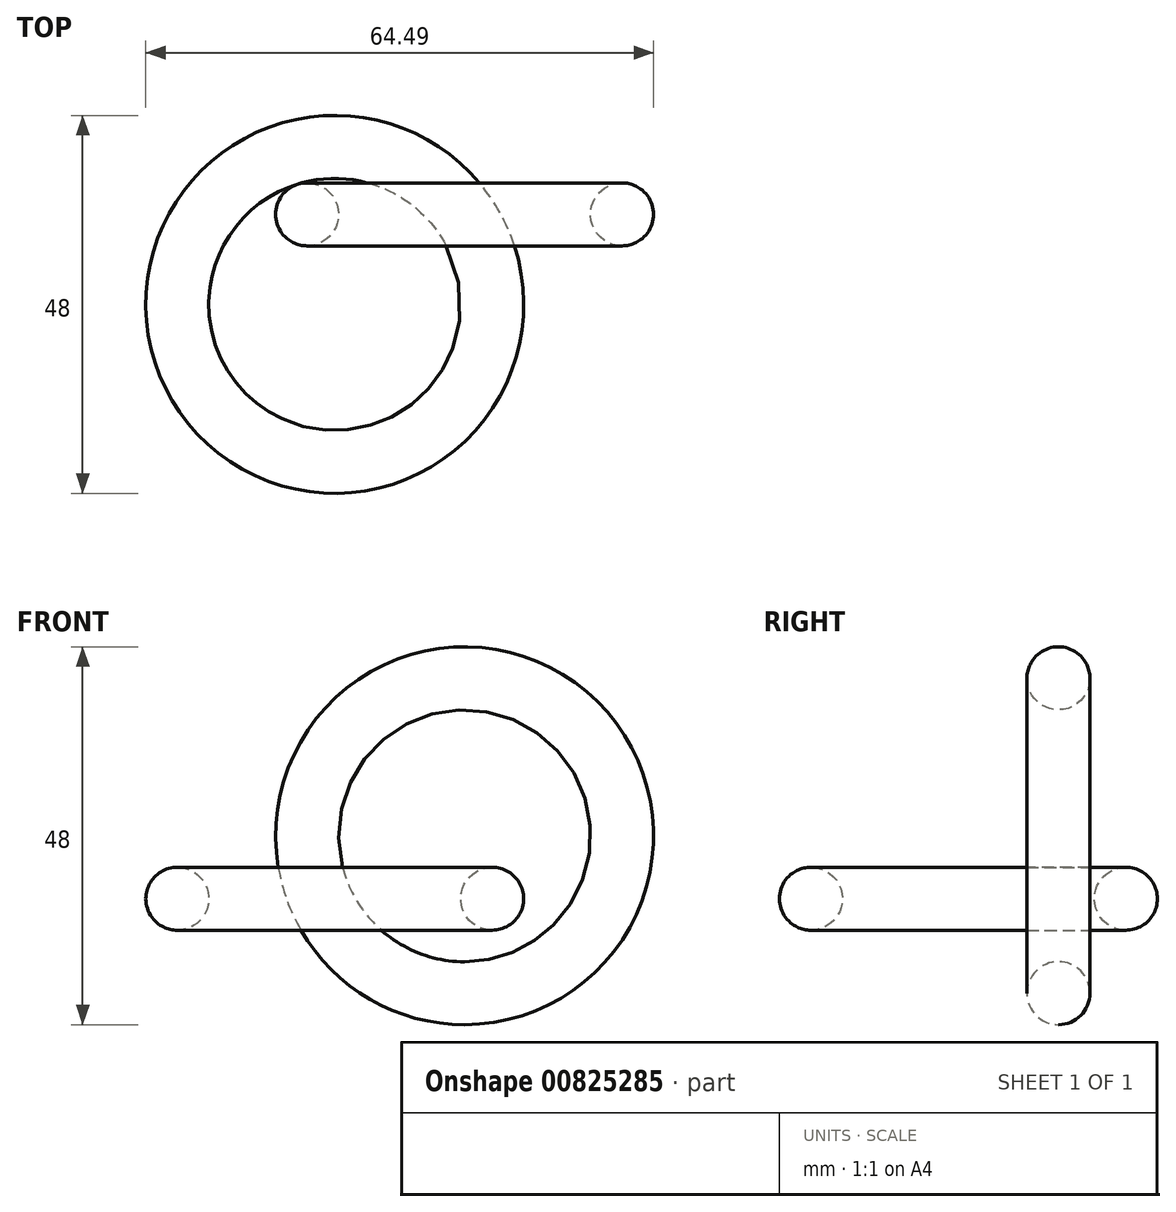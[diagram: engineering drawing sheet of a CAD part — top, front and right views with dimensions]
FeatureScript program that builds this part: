
annotation { "Feature Type Name" : "Feature", "Feature Type Description" : "" }
export const myFeature = defineFeature(function(context is Context, id is Id, definition is map)
    precondition{}
    {
        {
            var Q0;
            Q0=qCreatedBy(makeId("Top.planeOp"),FACE);
            var sketch = newSketch(context, id + "F0", { "sketchPlane" : qUnion([Q0])});
            skLineSegment(sketch, "E0", {"start": v(0, 0) * mm, "end": v(20, 0) * mm, "construction": true});
            skCircle(sketch, "E1", {"center": v(20, 0) * mm, "radius": 4 * mm});
            skSolve(sketch);
        }
        {
            var Q0;
            Q0=qCreatedBy(makeId("Front.planeOp"),FACE);
            var sketch = newSketch(context, id + "F1", { "sketchPlane" : qUnion([Q0])});
            skCircle(sketch, "E2", {"center": v(0, 0) * mm, "radius": 17.63 * mm});
            skSolve(sketch);
        }
        {
            var Q0;
            Q0=makeQuery(id+"F0.imprint","IMPRINT",FACE,{"disambiguationData":[TD([[makeQuery(id+"F0.imprint","IMPRINT",EDGE,{"derivedFrom":sQuery(id+"F0.wireOp",EDGE,"E1")}),1.0]])]});
            var Q1;
            Q1=sQuery(id+"F1.wireOp",EDGE,"E2");
            sweep(context, id + "F2", {"profiles" : qUnion([Q0]), "path" : qUnion([Q1])});
        }
        {
            var Q0;
            Q0=qCreatedBy(makeId("Front.planeOp"),FACE);
            var sketch = newSketch(context, id + "F3", { "sketchPlane" : qUnion([Q0])});
            skLineSegment(sketch, "E3", {"start": v(0, 0) * mm, "end": v(0, -1) * mm, "construction": true});
            skLineSegment(sketch, "E4.bottom", {"start": v(0, -1) * mm, "end": v(4, -1) * mm});
            skLineSegment(sketch, "E4.right", {"start": v(4, -1) * mm, "end": v(4, -21) * mm});
            skLineSegment(sketch, "E5.bottom", {"start": v(0, -1) * mm, "end": v(-4, -1) * mm});
            skLineSegment(sketch, "E5.top", {"start": v(0, -21) * mm, "end": v(-4, -21) * mm});
            skLineSegment(sketch, "E5.right", {"start": v(-4, -1) * mm, "end": v(-4, -21) * mm});
            skLineSegment(sketch, "E6", {"start": v(4, -21) * mm, "end": v(-4, -21) * mm});
            skSolve(sketch);
        }
        {
            var Q0;
            Q0=makeQuery(id+"F3.imprint","IMPRINT",FACE,{"disambiguationData":[TD([[makeQuery(id+"F3.imprint","IMPRINT",EDGE,{"derivedFrom":sQuery(id+"F3.wireOp",EDGE,"E4.bottom")}),-1.0]])]});
            extrude(context, id + "F4", {"entities" : qUnion([Q0]), "endBound" : BoundingType.SYMMETRIC, "oppositeDirection" : true, "depth" : 8 * mm, "offsetDistance" : 25 * mm});
        }
        {
            var Q0;
            Q0=makeQuery(id+"F4.opExtrude","CAP_EDGE",EDGE,{"disambiguationData":[OSD([sQuery(id+"F3.wireOp",EDGE,"E5.right")])],"isStart":false});
            chamfer(context, id + "F5", {"entities" : qUnion([Q0]), "width" : 8 * mm, "tangentPropagation" : true});
        }
        {
            var Q0;
            Q0=makeQuery(id+"F5.opChamfer","BLEND_FACE",FACE,{"disambiguationData":[OSD([sQuery(id+"F3.wireOp",EDGE,"E5.right")])]});
            var sketch = newSketch(context, id + "F6", { "sketchPlane" : qUnion([Q0])});
            skLineSegment(sketch, "E7", {"start": v(0, 0) * mm, "end": v(0, -8) * mm, "construction": true});
            skCircle(sketch, "E8", {"center": v(0, -8) * mm, "radius": 4 * mm});
            skSolve(sketch);
        }
        {
            var Q0;
            Q0=makeQuery(id+"F4.opExtrude","SWEPT_FACE",FACE,{"disambiguationData":[OSD([sQuery(id+"F3.wireOp",EDGE,"E6")])]});
            var sketch = newSketch(context, id + "F7", { "sketchPlane" : qUnion([Q0])});
            skLineSegment(sketch, "E9", {"start": v(0, 0) * mm, "end": v(-14.14, 14.14) * mm, "construction": true});
            skCircle(sketch, "E10", {"center": v(-14.14, 14.14) * mm, "radius": 20 * mm});
            skSolve(sketch);
        }
        {
            var Q0;
            {var subQ0=sQuery(id+"F6.wireOp",EDGE,"E8");var subQ1=makeQuery(id+"F5.opChamfer","BLEND_EDGE",EDGE,{"blendedFrom":[makeQuery(id+"F4.opExtrude","CAP_EDGE",EDGE,{"disambiguationData":[OSD([sQuery(id+"F3.wireOp",EDGE,"E5.right")])],"isStart":false}),makeQuery(id+"F4.opExtrude","SWEPT_FACE",FACE,{"disambiguationData":[OSD([sQuery(id+"F3.wireOp",EDGE,"E4.bottom"),sQuery(id+"F3.wireOp",EDGE,"E5.bottom")])]})],"blendedInto":[makeQuery(id+"F4.opExtrude","SWEPT_FACE",FACE,{"disambiguationData":[OSD([sQuery(id+"F3.wireOp",EDGE,"E4.bottom"),sQuery(id+"F3.wireOp",EDGE,"E5.bottom")])]})]});var subQ2=makeQuery(id+"F6.imprint","INTERSECT",VERTEX,{"disambiguationData":[OD(0.0)],"derivedFrom":[subQ1,subQ0]});Q0=makeQuery(id+"F6.imprint","IMPRINT",FACE,{"disambiguationData":[TD([[makeQuery(id+"F6.imprint","IMPRINT",EDGE,{"disambiguationData":[TD([[subQ2,1.0]])],"derivedFrom":subQ0}),1.0]])]});}
            var Q1;
            Q1=sQuery(id+"F7.wireOp",EDGE,"E10");
            sweep(context, id + "F8", {"profiles" : qUnion([Q0]), "path" : qUnion([Q1])});
        }
        {
            var Q0;
            Q0=makeQuery(id+"F8.opSweep","SWEPT_BODY",BODY,{"disambiguationData":[OSD([sQuery(id+"F6.wireOp",EDGE,"E8"),sQuery(id+"F7.wireOp",EDGE,"E10")])]});
            var Q1;
            Q1=makeQuery(id+"F5.opChamfer","BLEND_EDGE",EDGE,{"blendedFrom":[makeQuery(id+"F4.opExtrude","CAP_EDGE",EDGE,{"disambiguationData":[OSD([sQuery(id+"F3.wireOp",EDGE,"E5.right")])],"isStart":false}),makeQuery(id+"F4.opExtrude","SWEPT_FACE",FACE,{"disambiguationData":[OSD([sQuery(id+"F3.wireOp",EDGE,"E4.right")])]})],"blendedInto":[makeQuery(id+"F4.opExtrude","SWEPT_FACE",FACE,{"disambiguationData":[OSD([sQuery(id+"F3.wireOp",EDGE,"E4.right")])]})]});
            transform(context, id + "F9", {"entities" : qUnion([Q0]), "transformType" : TransformType.ROTATION, "transformAxis" : qUnion([Q1]), "angle" : 8 * degree, "makeCopy" : false});
        }
        {
            var Q0;
            Q0=makeQuery(id+"F4.opExtrude","SWEPT_BODY",BODY,{"disambiguationData":[OSD([sQuery(id+"F3.wireOp",EDGE,"E4.bottom"),sQuery(id+"F3.wireOp",EDGE,"E4.right"),sQuery(id+"F3.wireOp",EDGE,"E5.bottom"),sQuery(id+"F3.wireOp",EDGE,"E5.right"),sQuery(id+"F3.wireOp",EDGE,"E6")])]});
            deleteBodies(context, id + "F10", {"entities" : qUnion([Q0])});
        }
    });
